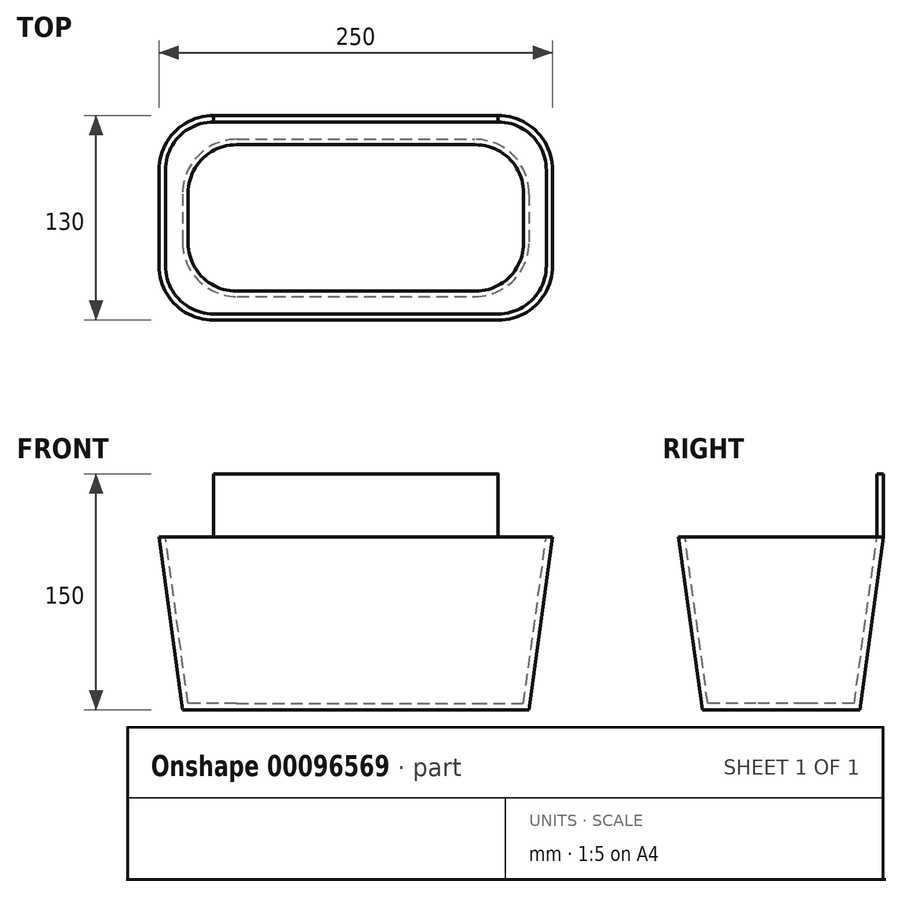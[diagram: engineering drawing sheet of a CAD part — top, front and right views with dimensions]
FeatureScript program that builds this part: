
annotation { "Feature Type Name" : "Feature", "Feature Type Description" : "" }
export const myFeature = defineFeature(function(context is Context, id is Id, definition is map)
    precondition{}
    {
        {
            var Q0;
            Q0=qCreatedBy(makeId("Front.planeOp"),FACE);
            var sketch = newSketch(context, id + "F0", { "sketchPlane" : qUnion([Q0])});
            skLineSegment(sketch, "E0.bottom", {"start": v(-125, 55) * mm, "end": v(0, 55) * mm});
            skLineSegment(sketch, "E0.top", {"start": v(-125, -55) * mm, "end": v(0, -55) * mm});
            skLineSegment(sketch, "E0.left", {"start": v(-125, 55) * mm, "end": v(-125, -55) * mm});
            skLineSegment(sketch, "E0.right", {"start": v(0, 55) * mm, "end": v(0, -55) * mm});
            skSolve(sketch);
        }
        {
            var Q0;
            Q0=makeQuery(id+"F0.imprint","IMPRINT",FACE,{"disambiguationData":[TD([[makeQuery(id+"F0.imprint","IMPRINT",EDGE,{"derivedFrom":sQuery(id+"F0.wireOp",EDGE,"E0.bottom")}),-1.0]])]});
            extrude(context, id + "F1", {"entities" : qUnion([Q0]), "depth" : 65 * mm});
        }
        {
            var Q0;
            Q0=makeQuery(id+"F1.opExtrude","CAP_FACE",FACE,{"disambiguationData":[OSD([sQuery(id+"F0.wireOp",EDGE,"E0.bottom"),sQuery(id+"F0.wireOp",EDGE,"E0.top"),sQuery(id+"F0.wireOp",EDGE,"E0.left"),sQuery(id+"F0.wireOp",EDGE,"E0.right")])],"isStart":false});
            var sketch = newSketch(context, id + "F2", { "sketchPlane" : qUnion([Q0])});
            skLineSegment(sketch, "E1", {"start": v(-62.5, 55) * mm, "end": v(-62.5, -55) * mm, "construction": true});
            skLineSegment(sketch, "E2", {"start": v(-125, 55) * mm, "end": v(-154.23, 55) * mm});
            skLineSegment(sketch, "E3", {"start": v(-154.23, 55) * mm, "end": v(-148.04, -67.18) * mm});
            skLineSegment(sketch, "E4", {"start": v(-148.04, -67.18) * mm, "end": v(-108, -65.15) * mm});
            skLineSegment(sketch, "E5", {"start": v(-108, -65.15) * mm, "end": v(-110, -55) * mm});
            skLineSegment(sketch, "E6", {"start": v(-125, 55) * mm, "end": v(-110, -55) * mm});
            skSolve(sketch);
        }
        {
            var Q0;
            Q0 = qSketchRegion(id + "F2", true);
            extrude(context, id + "F3", {"entities" : qUnion([Q0]), "operationType" : NewBodyOperationType.REMOVE, "endBound" : BoundingType.THROUGH_ALL, "oppositeDirection" : true, "depth" : 25 * mm});
        }
        {
            var Q0;
            Q0=makeQuery(id+"F1.opExtrude","SWEPT_FACE",FACE,{"disambiguationData":[OSD([sQuery(id+"F0.wireOp",EDGE,"E0.right")])]});
            var sketch = newSketch(context, id + "F4", { "sketchPlane" : qUnion([Q0])});
            skLineSegment(sketch, "E7", {"start": v(-65, 55) * mm, "end": v(-101.26, 55) * mm});
            skLineSegment(sketch, "E8", {"start": v(-101.26, 55) * mm, "end": v(-94.4, -57.44) * mm});
            skLineSegment(sketch, "E9", {"start": v(-94.4, -57.44) * mm, "end": v(-50, -57.44) * mm});
            skLineSegment(sketch, "E10", {"start": v(-50, -57.44) * mm, "end": v(-50, -55) * mm});
            skLineSegment(sketch, "E11", {"start": v(-65, 55) * mm, "end": v(-50, -55) * mm});
            skSolve(sketch);
        }
        {
            var Q0;
            Q0 = qSketchRegion(id + "F4", true);
            extrude(context, id + "F5", {"entities" : qUnion([Q0]), "operationType" : NewBodyOperationType.REMOVE, "endBound" : BoundingType.THROUGH_ALL, "oppositeDirection" : true, "depth" : 25 * mm});
        }
        {
            var Q0;
            Q0=makeQuery(id+"F1.opExtrude","SWEPT_BODY",BODY,{"disambiguationData":[OSD([sQuery(id+"F0.wireOp",EDGE,"E0.bottom"),sQuery(id+"F0.wireOp",EDGE,"E0.top"),sQuery(id+"F0.wireOp",EDGE,"E0.left"),sQuery(id+"F0.wireOp",EDGE,"E0.right")])]});
            var Q1;
            Q1=makeQuery(id+"F1.opExtrude","SWEPT_FACE",FACE,{"disambiguationData":[OSD([sQuery(id+"F0.wireOp",EDGE,"E0.right")])]});
            mirror(context, id + "F6", {"operationType" : NewBodyOperationType.ADD, "entities" : qUnion([Q0]), "mirrorPlane" : qUnion([Q1])});
        }
        {
            var Q0;
            Q0=makeQuery(id+"F1.opExtrude","SWEPT_BODY",BODY,{"disambiguationData":[OSD([sQuery(id+"F0.wireOp",EDGE,"E0.bottom"),sQuery(id+"F0.wireOp",EDGE,"E0.top"),sQuery(id+"F0.wireOp",EDGE,"E0.left"),sQuery(id+"F0.wireOp",EDGE,"E0.right")])]});
            var Q1;
            {var subQ0=makeQuery(id+"F1.opExtrude","CAP_FACE",FACE,{"disambiguationData":[OSD([sQuery(id+"F0.wireOp",EDGE,"E0.bottom"),sQuery(id+"F0.wireOp",EDGE,"E0.top"),sQuery(id+"F0.wireOp",EDGE,"E0.left"),sQuery(id+"F0.wireOp",EDGE,"E0.right")])],"isStart":true});Q1=makeQuery(id+"F6.boolean.opBoolean","MERGE",FACE,{"derivedFrom":[subQ0,makeQuery(id+"F6.opPattern","COPY",FACE,{"derivedFrom":subQ0,"instanceName":"1"})]});}
            mirror(context, id + "F7", {"operationType" : NewBodyOperationType.ADD, "entities" : qUnion([Q0]), "mirrorPlane" : qUnion([Q1])});
        }
        {
            var Q0;
            Q0=makeQuery(id+"F5.boolean.opBoolean","INTERSECT",EDGE,{"derivedFrom":[makeQuery(id+"F3.boolean.opBoolean","COPY",FACE,{"derivedFrom":makeQuery(id+"F3.opExtrude","SWEPT_FACE",FACE,{"disambiguationData":[OSD([sQuery(id+"F2.wireOp",EDGE,"E6")])]})}),makeQuery(id+"F5.opExtrude","SWEPT_FACE",FACE,{"disambiguationData":[OSD([sQuery(id+"F4.wireOp",EDGE,"E11")])]})]});
            var Q1;
            Q1=makeQuery(id+"F7.opPattern","COPY",EDGE,{"derivedFrom":makeQuery(id+"F5.boolean.opBoolean","INTERSECT",EDGE,{"derivedFrom":[makeQuery(id+"F3.boolean.opBoolean","COPY",FACE,{"derivedFrom":makeQuery(id+"F3.opExtrude","SWEPT_FACE",FACE,{"disambiguationData":[OSD([sQuery(id+"F2.wireOp",EDGE,"E6")])]})}),makeQuery(id+"F5.opExtrude","SWEPT_FACE",FACE,{"disambiguationData":[OSD([sQuery(id+"F4.wireOp",EDGE,"E11")])]})]}),"instanceName":"1"});
            var Q2;
            Q2=makeQuery(id+"F6.opPattern","COPY",EDGE,{"derivedFrom":makeQuery(id+"F5.boolean.opBoolean","INTERSECT",EDGE,{"derivedFrom":[makeQuery(id+"F3.boolean.opBoolean","COPY",FACE,{"derivedFrom":makeQuery(id+"F3.opExtrude","SWEPT_FACE",FACE,{"disambiguationData":[OSD([sQuery(id+"F2.wireOp",EDGE,"E6")])]})}),makeQuery(id+"F5.opExtrude","SWEPT_FACE",FACE,{"disambiguationData":[OSD([sQuery(id+"F4.wireOp",EDGE,"E11")])]})]}),"instanceName":"1"});
            var Q3;
            Q3=makeQuery(id+"F7.opPattern","COPY",EDGE,{"derivedFrom":makeQuery(id+"F6.opPattern","COPY",EDGE,{"derivedFrom":makeQuery(id+"F5.boolean.opBoolean","INTERSECT",EDGE,{"derivedFrom":[makeQuery(id+"F3.boolean.opBoolean","COPY",FACE,{"derivedFrom":makeQuery(id+"F3.opExtrude","SWEPT_FACE",FACE,{"disambiguationData":[OSD([sQuery(id+"F2.wireOp",EDGE,"E6")])]})}),makeQuery(id+"F5.opExtrude","SWEPT_FACE",FACE,{"disambiguationData":[OSD([sQuery(id+"F4.wireOp",EDGE,"E11")])]})]}),"instanceName":"1"}),"instanceName":"1"});
            fillet(context, id + "F8", {"entities" : qUnion([Q0, Q1, Q2, Q3]), "radius" : 35 * mm, "tangentPropagation" : true, "allowEdgeOverflow" : false});
        }
        {
            var Q0;
            {var subQ0=makeQuery(id+"F1.opExtrude","SWEPT_FACE",FACE,{"disambiguationData":[OSD([sQuery(id+"F0.wireOp",EDGE,"E0.bottom")])]});var subQ1=makeQuery(id+"F6.boolean.opBoolean","MERGE",FACE,{"derivedFrom":[subQ0,makeQuery(id+"F6.opPattern","COPY",FACE,{"derivedFrom":subQ0,"instanceName":"1"})]});Q0=makeQuery(id+"F7.boolean.opBoolean","MERGE",FACE,{"derivedFrom":[subQ1,makeQuery(id+"F7.opPattern","COPY",FACE,{"derivedFrom":subQ1,"instanceName":"1"})]});}
            shell(context, id + "F9", {"entities" : qUnion([Q0]), "thickness" : 4 * mm});
        }
        {
            var Q0;
            {var subQ0=makeQuery(id+"F1.opExtrude","SWEPT_FACE",FACE,{"disambiguationData":[OSD([sQuery(id+"F0.wireOp",EDGE,"E0.bottom")])]});var subQ1=makeQuery(id+"F6.boolean.opBoolean","MERGE",FACE,{"derivedFrom":[subQ0,makeQuery(id+"F6.opPattern","COPY",FACE,{"derivedFrom":subQ0,"instanceName":"1"})]});Q0=makeQuery(id+"F7.boolean.opBoolean","MERGE",FACE,{"derivedFrom":[subQ1,makeQuery(id+"F7.opPattern","COPY",FACE,{"derivedFrom":subQ1,"instanceName":"1"})]});}
            var sketch = newSketch(context, id + "F10", { "sketchPlane" : qUnion([Q0])});
            skLineSegment(sketch, "E12.bottom", {"start": v(90.32, 65) * mm, "end": v(-90.32, 65) * mm});
            skLineSegment(sketch, "E12.top", {"start": v(90.32, 60.96) * mm, "end": v(-90.32, 60.96) * mm});
            skLineSegment(sketch, "E12.left", {"start": v(90.32, 65) * mm, "end": v(90.32, 60.96) * mm});
            skLineSegment(sketch, "E12.right", {"start": v(-90.32, 65) * mm, "end": v(-90.32, 60.96) * mm});
            skSolve(sketch);
        }
        {
            var Q0;
            Q0 = qSketchRegion(id + "F10", true);
            extrude(context, id + "F11", {"entities" : qUnion([Q0]), "operationType" : NewBodyOperationType.ADD, "depth" : 40 * mm});
        }
    });
